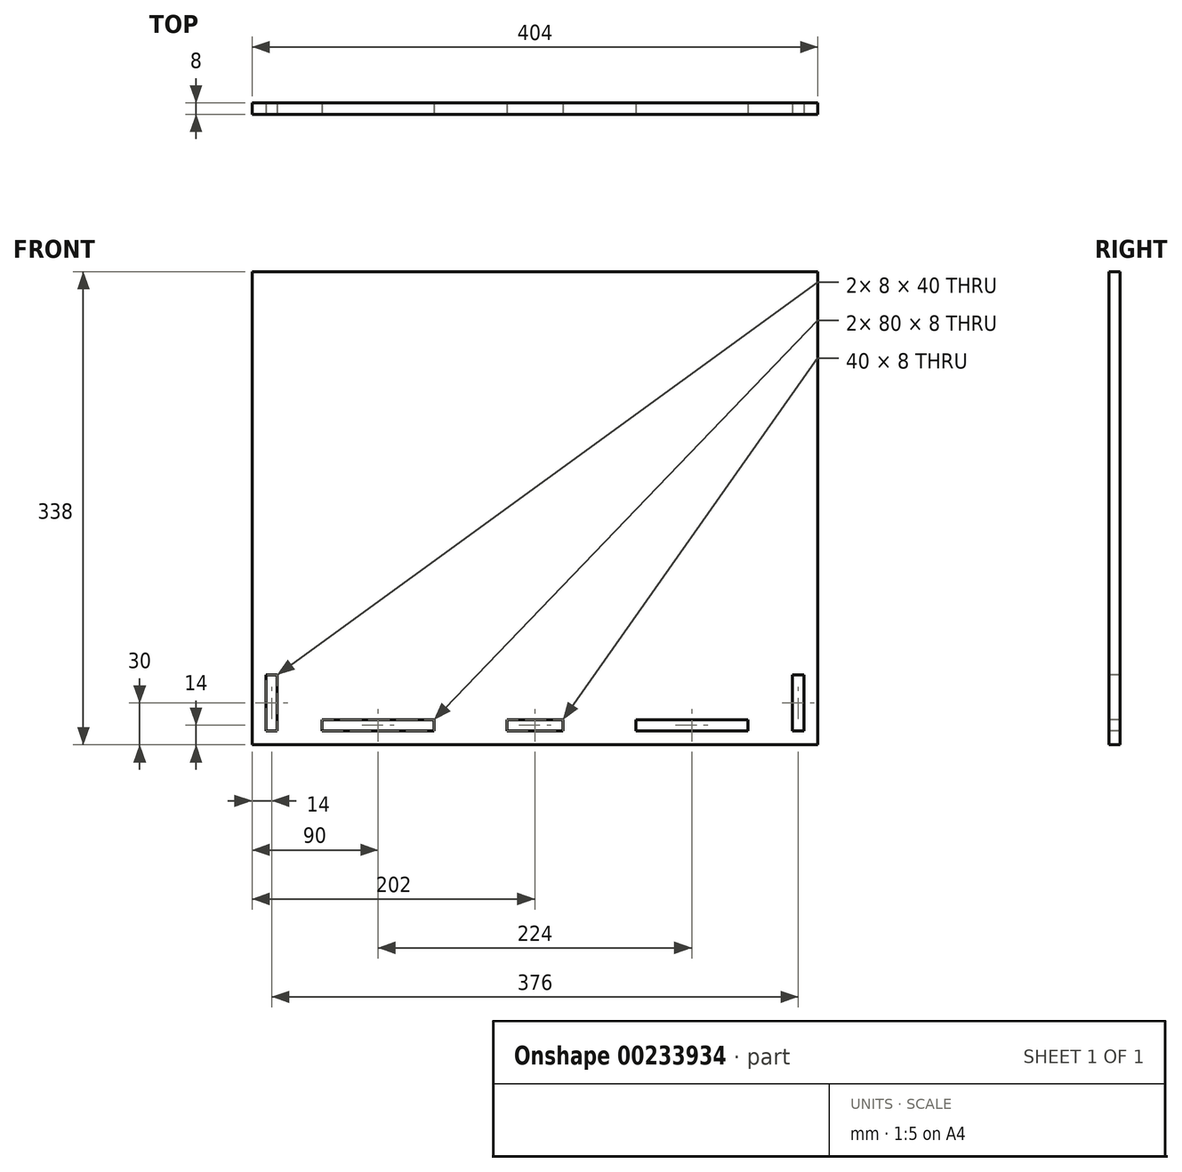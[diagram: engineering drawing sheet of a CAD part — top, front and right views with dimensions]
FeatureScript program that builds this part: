
annotation { "Feature Type Name" : "Feature", "Feature Type Description" : "" }
export const myFeature = defineFeature(function(context is Context, id is Id, definition is map)
    precondition{}
    {
        {
            var Q0;
            Q0=qCreatedBy(makeId("Front.planeOp"),FACE);
            var sketch = newSketch(context, id + "F0", { "sketchPlane" : qUnion([Q0])});
            skLineSegment(sketch, "E0.bottom", {"start": v(0, 0) * mm, "end": v(404, 0) * mm});
            skLineSegment(sketch, "E0.top", {"start": v(0, 338) * mm, "end": v(404, 338) * mm});
            skLineSegment(sketch, "E0.left", {"start": v(0, 0) * mm, "end": v(0, 338) * mm});
            skLineSegment(sketch, "E0.right", {"start": v(404, 0) * mm, "end": v(404, 338) * mm});
            skLineSegment(sketch, "E1", {"start": v(10, 10) * mm, "end": v(18, 10) * mm});
            skLineSegment(sketch, "E2", {"start": v(18, 10) * mm, "end": v(18, 50) * mm});
            skLineSegment(sketch, "E3", {"start": v(18, 50) * mm, "end": v(10, 50) * mm});
            skLineSegment(sketch, "E4", {"start": v(10, 50) * mm, "end": v(10, 10) * mm});
            skLineSegment(sketch, "E5.bottom", {"start": v(394, 10) * mm, "end": v(386, 10) * mm});
            skLineSegment(sketch, "E5.top", {"start": v(394, 50) * mm, "end": v(386, 50) * mm});
            skLineSegment(sketch, "E5.left", {"start": v(394, 10) * mm, "end": v(394, 50) * mm});
            skLineSegment(sketch, "E5.right", {"start": v(386, 10) * mm, "end": v(386, 50) * mm});
            skLineSegment(sketch, "E6.bottom", {"start": v(50, 10) * mm, "end": v(130, 10) * mm});
            skLineSegment(sketch, "E6.top", {"start": v(50, 18) * mm, "end": v(130, 18) * mm});
            skLineSegment(sketch, "E6.left", {"start": v(50, 10) * mm, "end": v(50, 18) * mm});
            skLineSegment(sketch, "E6.right", {"start": v(130, 10) * mm, "end": v(130, 18) * mm});
            skLineSegment(sketch, "E7.bottom", {"start": v(274, 18) * mm, "end": v(354, 18) * mm});
            skLineSegment(sketch, "E7.top", {"start": v(274, 10) * mm, "end": v(354, 10) * mm});
            skLineSegment(sketch, "E7.left", {"start": v(274, 18) * mm, "end": v(274, 10) * mm});
            skLineSegment(sketch, "E7.right", {"start": v(354, 18) * mm, "end": v(354, 10) * mm});
            skLineSegment(sketch, "E8.bottom", {"start": v(182, 18) * mm, "end": v(222, 18) * mm});
            skLineSegment(sketch, "E8.top", {"start": v(182, 10) * mm, "end": v(222, 10) * mm});
            skLineSegment(sketch, "E8.left", {"start": v(182, 18) * mm, "end": v(182, 10) * mm});
            skLineSegment(sketch, "E8.right", {"start": v(222, 18) * mm, "end": v(222, 10) * mm});
            skSolve(sketch);
        }
        {
            var Q0;
            Q0=makeQuery(id+"F0.imprint","IMPRINT",FACE,{"disambiguationData":[TD([[makeQuery(id+"F0.imprint","IMPRINT",EDGE,{"derivedFrom":sQuery(id+"F0.wireOp",EDGE,"E0.bottom")}),1.0]])]});
            extrude(context, id + "F1", {"entities" : qUnion([Q0]), "oppositeDirection" : true, "depth" : 8 * mm});
        }
    });
